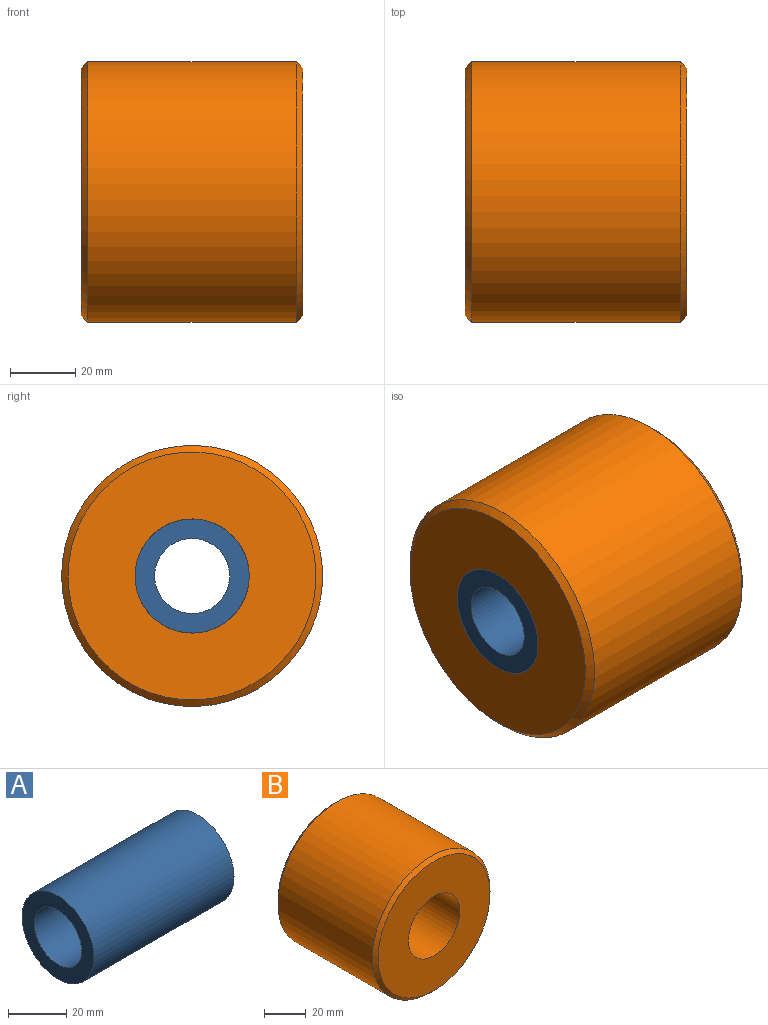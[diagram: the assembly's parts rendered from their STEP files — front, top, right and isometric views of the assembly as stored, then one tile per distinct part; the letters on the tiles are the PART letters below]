
ASSEMBLY  parts=2 mates=1
PART A: 4 faces, bbox 68x35x35 mm
  f0: cylinder r=11.5mm len=68mm, axis (-1,0,0), area 4913.5mm2, adj f2,f3
  f1: cylinder r=17.5mm len=68mm, axis (-1,0,0), area 7477mm2, adj f2,f3
  f2: plane 35x35mm, normal (1,0,0), area 546.6mm2, adj f0,f1
  f3: plane 35x35mm, normal (-1,0,0), area 546.6mm2, adj f0,f1
PART B: 6 faces, bbox 80x68x80 mm
  f0: cylinder r=17.5mm len=68mm, axis (0,1,0), area 7477mm2, adj f2,f3
  f1: cylinder r=40mm len=80mm, axis (0,1,0), area 16085mm2, adj f4,f5
  f2: plane 76x76mm, normal (0,-1,0), area 3574.3mm2, adj f0,f4
  f3: plane 76x76mm, normal (0,1,0), area 3574.3mm2, adj f0,f5
  f4: cone r=38mm half-angle=45deg, axis (0,1,0), area 693.1mm2, adj f1,f2
  f5: cone r=40mm half-angle=45deg, axis (0,-1,0), area 693.1mm2, adj f1,f3
PLACE A t=(-39.92,-16.44,-48.98)mm
PLACE B rot(axis=(0.58,-0.58,0.58),120deg) t=(-39.92,-16.44,-48.98)mm
MATE fastened A.f0 <-> B.f0  axis (-1,0,0) through (28.08,-16.44,-48.98)mm
